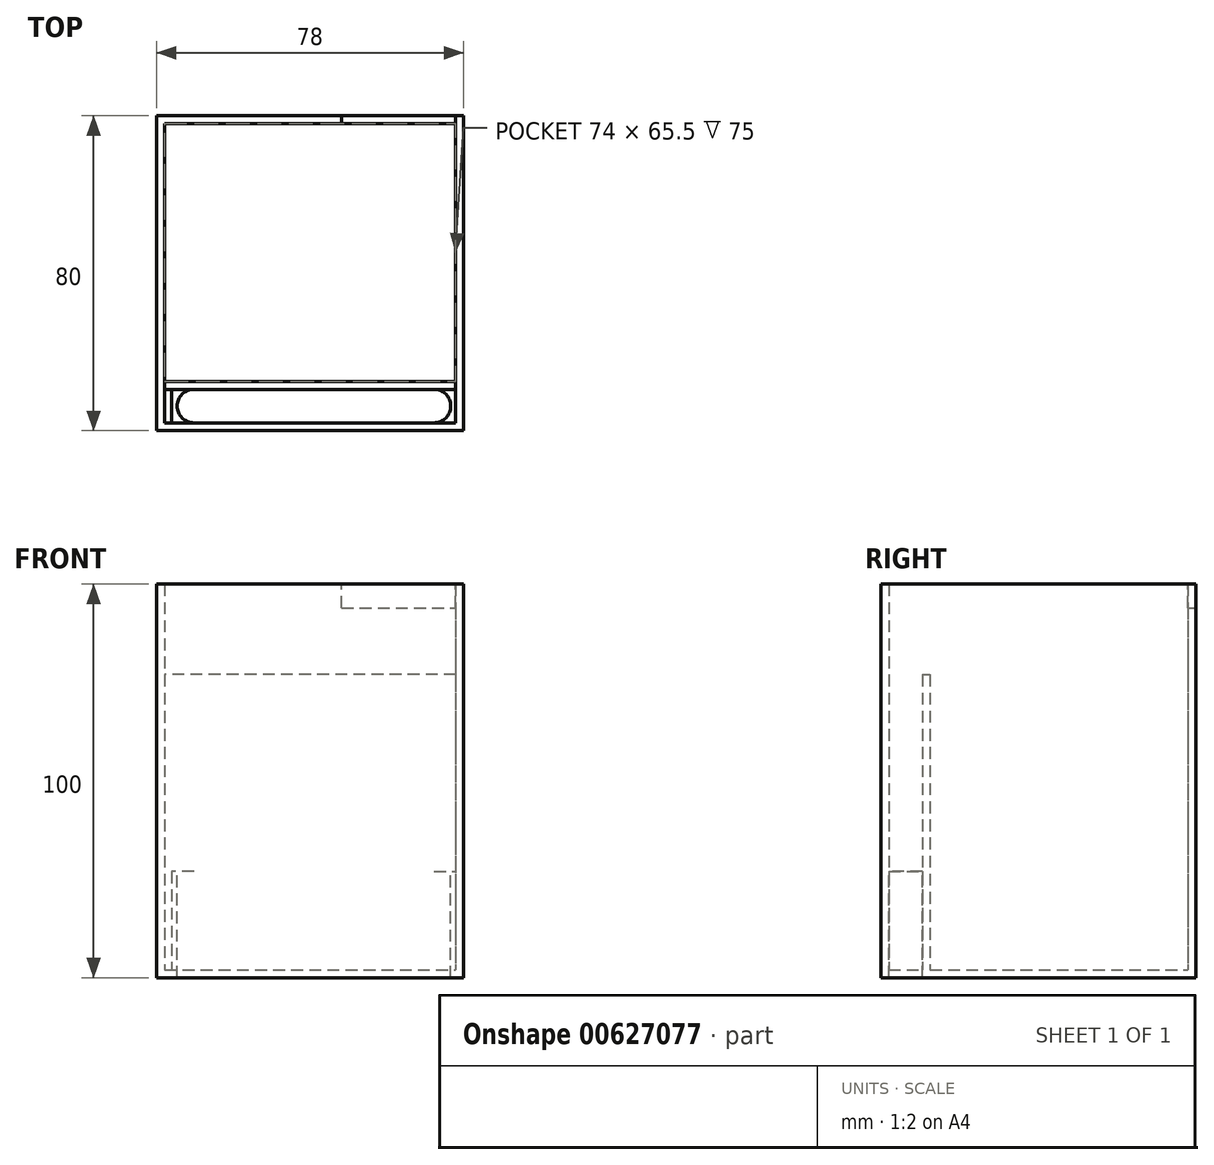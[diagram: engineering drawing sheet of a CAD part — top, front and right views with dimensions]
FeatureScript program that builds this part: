
annotation { "Feature Type Name" : "Feature", "Feature Type Description" : "" }
export const myFeature = defineFeature(function(context is Context, id is Id, definition is map)
    precondition{}
    {
        {
            var Q0;
            Q0=qCreatedBy(makeId("Top.planeOp"),FACE);
            var sketch = newSketch(context, id + "F0", { "sketchPlane" : qUnion([Q0])});
            skLineSegment(sketch, "E0.bottom", {"start": v(0, 0) * mm, "end": v(78, 0) * mm});
            skLineSegment(sketch, "E0.top", {"start": v(0, 80) * mm, "end": v(78, 80) * mm});
            skLineSegment(sketch, "E0.left", {"start": v(0, 0) * mm, "end": v(0, 80) * mm});
            skLineSegment(sketch, "E0.right", {"start": v(78, 0) * mm, "end": v(78, 80) * mm});
            skSolve(sketch);
        }
        {
            var Q0;
            Q0 = qSketchRegion(id + "F0", true);
            extrude(context, id + "F1", {"entities" : qUnion([Q0]), "depth" : 100 * mm, "offsetDistance" : 25 * mm});
        }
        {
            var Q0;
            Q0=makeQuery(id+"F1.opExtrude","CAP_FACE",FACE,{"disambiguationData":[OSD([sQuery(id+"F0.wireOp",EDGE,"E0.bottom"),sQuery(id+"F0.wireOp",EDGE,"E0.top"),sQuery(id+"F0.wireOp",EDGE,"E0.left"),sQuery(id+"F0.wireOp",EDGE,"E0.right")])],"isStart":false});
            shell(context, id + "F2", {"entities" : qUnion([Q0]), "thickness" : 2 * mm});
        }
        {
            var Q0;
            Q0=makeQuery(id+"F2.opShell","OFFSET_FACE",FACE,{"disambiguationData":[OSD([sQuery(id+"F0.wireOp",EDGE,"E0.bottom"),sQuery(id+"F0.wireOp",EDGE,"E0.top"),sQuery(id+"F0.wireOp",EDGE,"E0.left"),sQuery(id+"F0.wireOp",EDGE,"E0.right")])]});
            var sketch = newSketch(context, id + "F3", { "sketchPlane" : qUnion([Q0])});
            skLineSegment(sketch, "E1", {"start": v(76, 2) * mm, "end": v(76, 10.5) * mm, "construction": true});
            skLineSegment(sketch, "E2", {"start": v(76, 10.5) * mm, "end": v(2, 10.5) * mm});
            skLineSegment(sketch, "E3", {"start": v(2, 10.5) * mm, "end": v(2, 12.5) * mm});
            skLineSegment(sketch, "E4", {"start": v(2, 12.5) * mm, "end": v(76, 12.5) * mm});
            skLineSegment(sketch, "E5", {"start": v(76, 12.5) * mm, "end": v(76, 10.5) * mm});
            skSolve(sketch);
        }
        {
            var Q0;
            Q0 = qSketchRegion(id + "F3", true);
            extrude(context, id + "F4", {"entities" : qUnion([Q0]), "operationType" : NewBodyOperationType.ADD, "depth" : 75 * mm, "offsetDistance" : 25 * mm});
        }
        {
            var Q0;
            Q0=makeQuery(id+"F2.opShell","OFFSET_FACE",FACE,{"disambiguationData":[OSD([sQuery(id+"F0.wireOp",EDGE,"E0.bottom"),sQuery(id+"F0.wireOp",EDGE,"E0.top"),sQuery(id+"F0.wireOp",EDGE,"E0.left"),sQuery(id+"F0.wireOp",EDGE,"E0.right")])]});
            var sketch = newSketch(context, id + "F5", { "sketchPlane" : qUnion([Q0])});
            skLineSegment(sketch, "E6.bottom", {"start": v(76, 2) * mm, "end": v(3.82, 2) * mm});
            skLineSegment(sketch, "E6.top", {"start": v(76, 11.1) * mm, "end": v(3.82, 11.1) * mm});
            skLineSegment(sketch, "E6.left", {"start": v(76, 2) * mm, "end": v(76, 11.1) * mm});
            skLineSegment(sketch, "E6.right", {"start": v(3.82, 2) * mm, "end": v(3.82, 11.1) * mm});
            skSolve(sketch);
        }
        {
            var Q0;
            Q0 = qSketchRegion(id + "F5", true);
            extrude(context, id + "F6", {"entities" : qUnion([Q0]), "operationType" : NewBodyOperationType.ADD, "depth" : 25 * mm, "offsetDistance" : 25 * mm});
        }
        {
            var Q0;
            Q0=makeQuery(id+"F6.opExtrude","CAP_FACE",FACE,{"disambiguationData":[OSD([sQuery(id+"F5.wireOp",EDGE,"E6.bottom"),sQuery(id+"F5.wireOp",EDGE,"E6.top"),sQuery(id+"F5.wireOp",EDGE,"E6.left"),sQuery(id+"F5.wireOp",EDGE,"E6.right")])],"isStart":false});
            var sketch = newSketch(context, id + "F7", { "sketchPlane" : qUnion([Q0])});
            skLineSegment(sketch, "E7", {"start": v(2.47, 10.5) * mm, "end": v(9.47, 10.5) * mm, "construction": true});
            skLineSegment(sketch, "E8", {"start": v(9.47, 10.5) * mm, "end": v(9.47, 2) * mm, "construction": true});
            skArc(sketch, "E9", {"start": v(9.47, 10.5) * mm, "mid": v(5.22, 6.25) * mm, "end": v(9.47, 2) * mm});
            skLineSegment(sketch, "E10", {"start": v(76.47, 10.5) * mm, "end": v(70.47, 10.5) * mm, "construction": true});
            skLineSegment(sketch, "E11", {"start": v(70.47, 10.5) * mm, "end": v(70.47, 2) * mm, "construction": true});
            skArc(sketch, "E12", {"start": v(70.47, 2) * mm, "mid": v(74.72, 6.25) * mm, "end": v(70.47, 10.5) * mm});
            skLineSegment(sketch, "E13", {"start": v(70.47, 10.5) * mm, "end": v(9.47, 10.5) * mm});
            skLineSegment(sketch, "E14", {"start": v(9.47, 2) * mm, "end": v(70.47, 2) * mm});
            skSolve(sketch);
        }
        {
            var Q0;
            Q0 = qSketchRegion(id + "F7", true);
            extrude(context, id + "F8", {"entities" : qUnion([Q0]), "operationType" : NewBodyOperationType.REMOVE, "oppositeDirection" : true, "depth" : 38.5 * mm, "offsetDistance" : 25 * mm});
        }
        {
            var Q0;
            Q0=makeQuery(id+"F1.opExtrude","CAP_FACE",FACE,{"disambiguationData":[OSD([sQuery(id+"F0.wireOp",EDGE,"E0.bottom"),sQuery(id+"F0.wireOp",EDGE,"E0.top"),sQuery(id+"F0.wireOp",EDGE,"E0.left"),sQuery(id+"F0.wireOp",EDGE,"E0.right")])],"isStart":false});
            var sketch = newSketch(context, id + "F9", { "sketchPlane" : qUnion([Q0])});
            skLineSegment(sketch, "E15.bottom", {"start": v(76, 78) * mm, "end": v(47, 78) * mm});
            skLineSegment(sketch, "E15.top", {"start": v(76, 80) * mm, "end": v(47, 80) * mm});
            skLineSegment(sketch, "E15.left", {"start": v(76, 78) * mm, "end": v(76, 80) * mm});
            skLineSegment(sketch, "E15.right", {"start": v(47, 78) * mm, "end": v(47, 80) * mm});
            skSolve(sketch);
        }
        {
            var Q0;
            Q0 = qSketchRegion(id + "F9", true);
            extrude(context, id + "F10", {"entities" : qUnion([Q0]), "operationType" : NewBodyOperationType.REMOVE, "oppositeDirection" : true, "depth" : 6 * mm, "offsetDistance" : 25 * mm});
        }
    });
